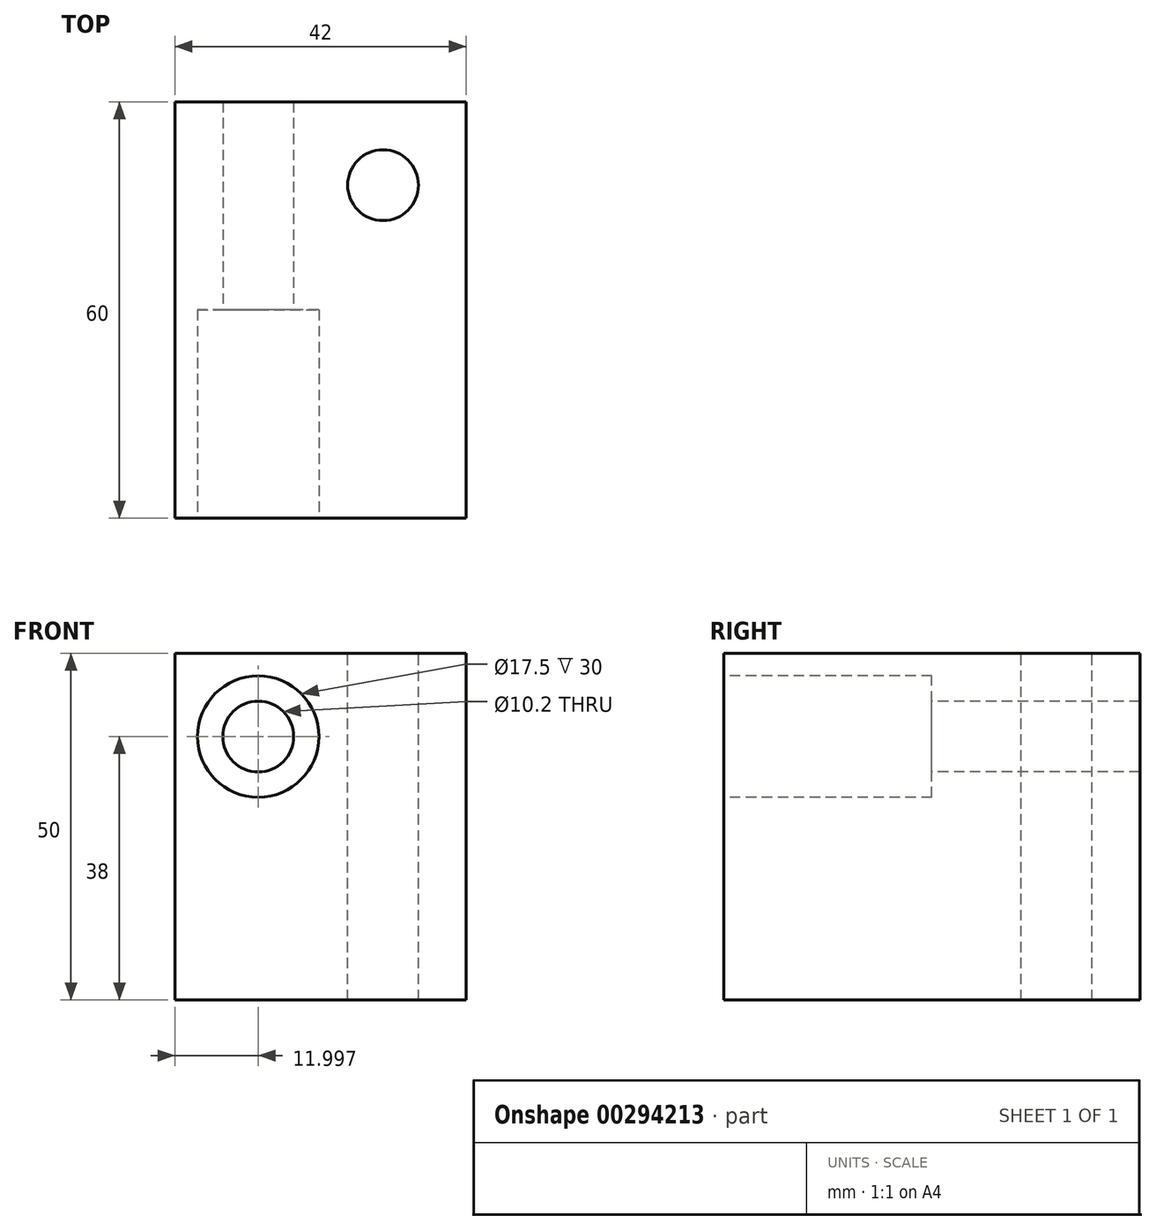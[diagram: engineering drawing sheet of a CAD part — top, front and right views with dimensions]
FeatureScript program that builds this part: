
annotation { "Feature Type Name" : "Feature", "Feature Type Description" : "" }
export const myFeature = defineFeature(function(context is Context, id is Id, definition is map)
    precondition{}
    {
        {
            var Q0;
            Q0=qCreatedBy(makeId("Top.planeOp"),FACE);
            var sketch = newSketch(context, id + "F0", { "sketchPlane" : qUnion([Q0])});
            skLineSegment(sketch, "E0", {"start": v(-51.52, 34.61) * mm, "end": v(-51.52, -25.39) * mm});
            skLineSegment(sketch, "E1", {"start": v(-51.52, -25.39) * mm, "end": v(-9.52, -25.39) * mm});
            skLineSegment(sketch, "E2", {"start": v(-9.52, -25.39) * mm, "end": v(-9.52, 34.61) * mm});
            skLineSegment(sketch, "E3", {"start": v(-9.52, 34.61) * mm, "end": v(-51.52, 34.61) * mm});
            skSolve(sketch);
        }
        {
            var Q0;
            Q0=makeQuery(id+"F0.imprint","IMPRINT",FACE,{"disambiguationData":[TD([[makeQuery(id+"F0.imprint","IMPRINT",EDGE,{"derivedFrom":sQuery(id+"F0.wireOp",EDGE,"E0")}),1.0]])]});
            extrude(context, id + "F1", {"entities" : qUnion([Q0]), "depth" : 25 * mm});
        }
        {
            var Q0;
            Q0=makeQuery(id+"F1.opExtrude","CAP_FACE",FACE,{"disambiguationData":[OSD([sQuery(id+"F0.wireOp",EDGE,"E0"),sQuery(id+"F0.wireOp",EDGE,"E1"),sQuery(id+"F0.wireOp",EDGE,"E2"),sQuery(id+"F0.wireOp",EDGE,"E3")])],"isStart":false});
            var sketch = newSketch(context, id + "F2", { "sketchPlane" : qUnion([Q0])});
            skCircle(sketch, "E4", {"center": v(-21.52, 22.61) * mm, "radius": 5.1 * mm});
            skSolve(sketch);
        }
        {
            var Q0;
            Q0=makeQuery(id+"F2.imprint","IMPRINT",FACE,{"disambiguationData":[TD([[makeQuery(id+"F2.imprint","IMPRINT",EDGE,{"derivedFrom":sQuery(id+"F2.wireOp",EDGE,"E4")}),1.0]])]});
            extrude(context, id + "F3", {"entities" : qUnion([Q0]), "operationType" : NewBodyOperationType.REMOVE, "endBound" : BoundingType.THROUGH_ALL, "oppositeDirection" : true, "depth" : 25 * mm});
        }
        {
            var Q0;
            Q0=makeQuery(id+"F1.opExtrude","CAP_FACE",FACE,{"disambiguationData":[OSD([sQuery(id+"F0.wireOp",EDGE,"E0"),sQuery(id+"F0.wireOp",EDGE,"E1"),sQuery(id+"F0.wireOp",EDGE,"E2"),sQuery(id+"F0.wireOp",EDGE,"E3")])],"isStart":false});
            extrude(context, id + "F4", {"entities" : qUnion([Q0]), "operationType" : NewBodyOperationType.ADD, "depth" : 25 * mm});
        }
        {
            var Q0;
            {var subQ0=sQuery(id+"F0.wireOp",EDGE,"E1");Q0=makeQuery(id+"F4.boolean.opBoolean","MERGE",FACE,{"derivedFrom":[makeQuery(id+"F1.opExtrude","SWEPT_FACE",FACE,{"disambiguationData":[OSD([subQ0])]}),makeQuery(id+"F4.opExtrude","SWEPT_FACE",FACE,{"disambiguationData":[OSD([subQ0])]})]});}
            var sketch = newSketch(context, id + "F5", { "sketchPlane" : qUnion([Q0])});
            skCircle(sketch, "E5", {"center": v(-39.52, 38) * mm, "radius": 8.75 * mm});
            skSolve(sketch);
        }
        {
            var Q0;
            Q0=makeQuery(id+"F5.imprint","IMPRINT",FACE,{"disambiguationData":[TD([[makeQuery(id+"F5.imprint","IMPRINT",EDGE,{"derivedFrom":sQuery(id+"F5.wireOp",EDGE,"E5")}),1.0]])]});
            extrude(context, id + "F6", {"entities" : qUnion([Q0]), "operationType" : NewBodyOperationType.REMOVE, "oppositeDirection" : true, "depth" : 30 * mm});
        }
        {
            var Q0;
            Q0=makeQuery(id+"F6.boolean.opBoolean","COPY",FACE,{"derivedFrom":makeQuery(id+"F6.opExtrude","CAP_FACE",FACE,{"disambiguationData":[OSD([sQuery(id+"F5.wireOp",EDGE,"E5")])],"isStart":false})});
            var sketch = newSketch(context, id + "F7", { "sketchPlane" : qUnion([Q0])});
            skCircle(sketch, "E6", {"center": v(-39.52, 38) * mm, "radius": 5.1 * mm});
            skSolve(sketch);
        }
        {
            var Q0;
            Q0=makeQuery(id+"F7.imprint","IMPRINT",FACE,{"disambiguationData":[TD([[makeQuery(id+"F7.imprint","IMPRINT",EDGE,{"derivedFrom":sQuery(id+"F7.wireOp",EDGE,"E6")}),1.0]])]});
            extrude(context, id + "F8", {"entities" : qUnion([Q0]), "operationType" : NewBodyOperationType.REMOVE, "oppositeDirection" : true, "depth" : 60 * mm});
        }
    });
